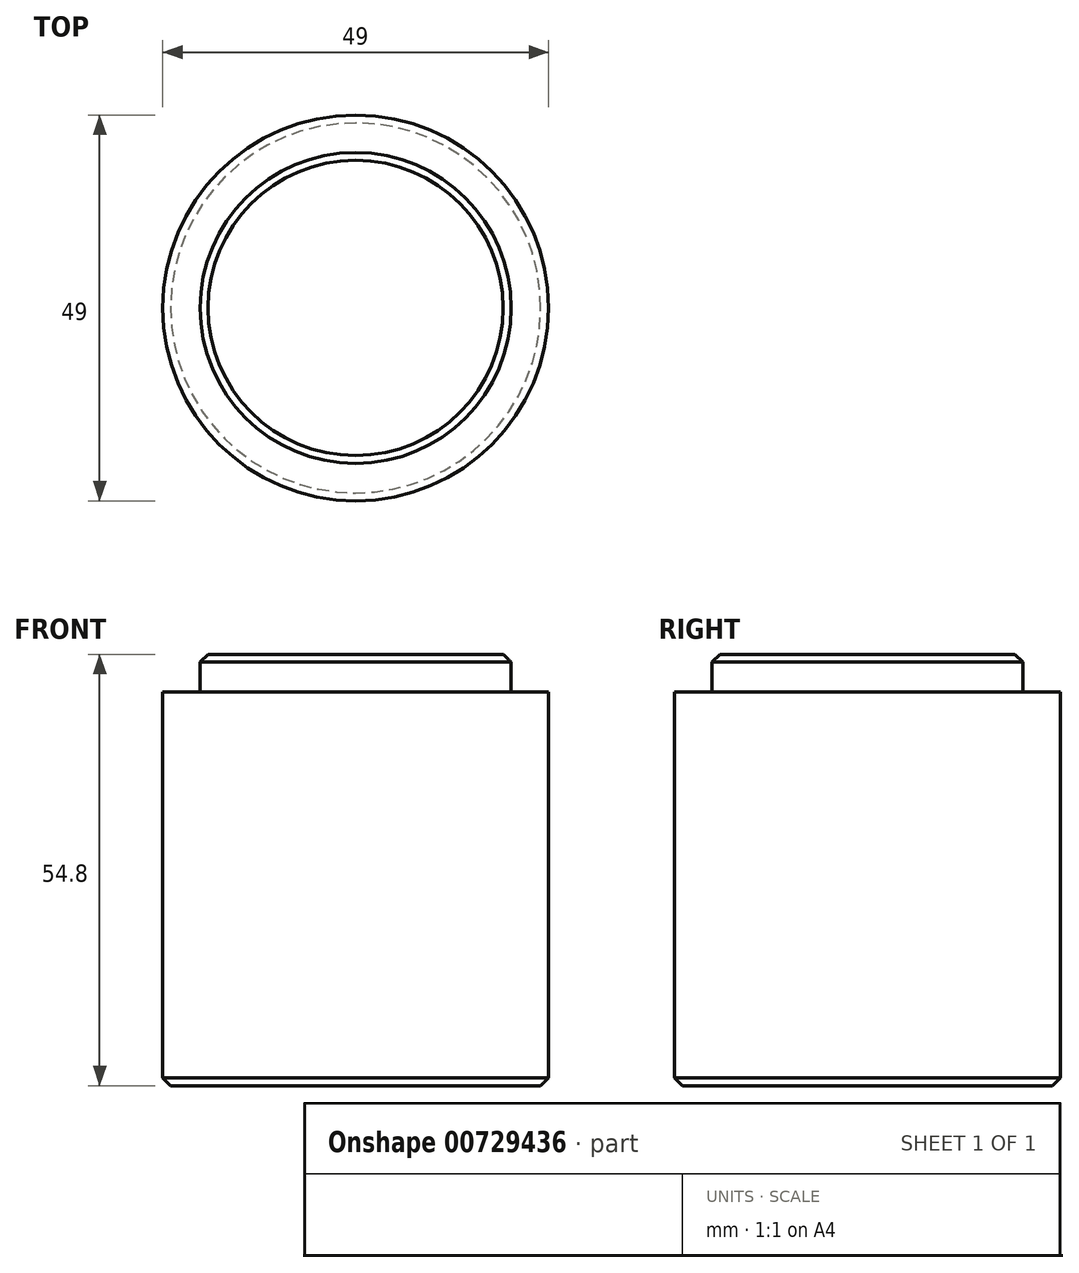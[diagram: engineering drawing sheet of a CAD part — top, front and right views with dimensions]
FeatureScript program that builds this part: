
annotation { "Feature Type Name" : "Feature", "Feature Type Description" : "" }
export const myFeature = defineFeature(function(context is Context, id is Id, definition is map)
    precondition{}
    {
        {
            var Q0;
            Q0=qCreatedBy(makeId("Top.planeOp"),FACE);
            var sketch = newSketch(context, id + "F0", { "sketchPlane" : qUnion([Q0])});
            skCircle(sketch, "E0", {"center": v(0, 0) * mm, "radius": 24.5 * mm});
            skSolve(sketch);
        }
        {
            var Q0;
            Q0=makeQuery(id+"F0.imprint","IMPRINT",FACE,{"disambiguationData":[TD([[makeQuery(id+"F0.imprint","IMPRINT",EDGE,{"derivedFrom":sQuery(id+"F0.wireOp",EDGE,"E0")}),1.0]])]});
            extrude(context, id + "F1", {"entities" : qUnion([Q0]), "depth" : 50 * mm, "offsetDistance" : 25 * mm});
        }
        {
            var Q0;
            Q0=makeQuery(id+"F1.opExtrude","CAP_FACE",FACE,{"disambiguationData":[OSD([sQuery(id+"F0.wireOp",EDGE,"E0")])],"isStart":false});
            var sketch = newSketch(context, id + "F2", { "sketchPlane" : qUnion([Q0])});
            skCircle(sketch, "E1", {"center": v(0, 0) * mm, "radius": 19.75 * mm});
            skSolve(sketch);
        }
        {
            var Q0;
            Q0=makeQuery(id+"F2.imprint","IMPRINT",FACE,{"disambiguationData":[TD([[makeQuery(id+"F2.imprint","IMPRINT",EDGE,{"derivedFrom":sQuery(id+"F2.wireOp",EDGE,"E1")}),1.0]])]});
            extrude(context, id + "F3", {"entities" : qUnion([Q0]), "operationType" : NewBodyOperationType.ADD, "depth" : 4.8 * mm, "offsetDistance" : 25 * mm});
        }
        {
            var Q0;
            Q0=makeQuery(id+"F1.opExtrude","CAP_EDGE",EDGE,{"disambiguationData":[OSD([sQuery(id+"F0.wireOp",EDGE,"E0")])],"isStart":true});
            var Q1;
            Q1=makeQuery(id+"F3.opExtrude","CAP_EDGE",EDGE,{"disambiguationData":[OSD([sQuery(id+"F2.wireOp",EDGE,"E1")])],"isStart":false});
            chamfer(context, id + "F4", {"entities" : qUnion([Q0, Q1]), "width" : 1 * mm, "tangentPropagation" : true});
        }
    });
